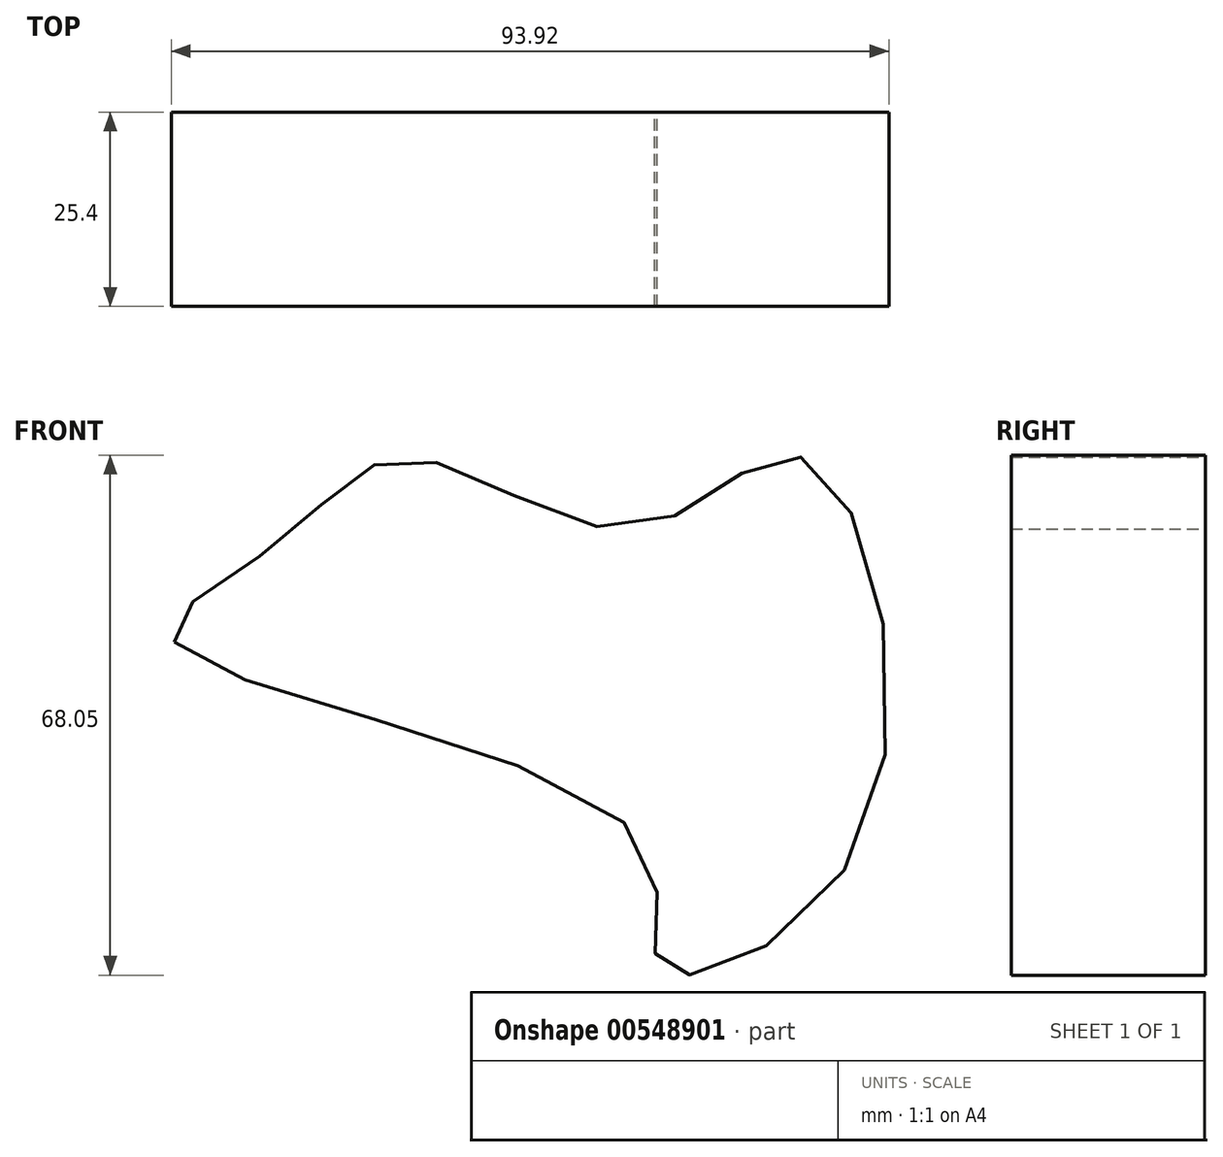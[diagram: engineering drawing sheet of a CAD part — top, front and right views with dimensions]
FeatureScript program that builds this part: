
annotation { "Feature Type Name" : "Feature", "Feature Type Description" : "" }
export const myFeature = defineFeature(function(context is Context, id is Id, definition is map)
    precondition{}
    {
        {
            var Q0;
            Q0=qCreatedBy(makeId("Front.planeOp"),FACE);
            var sketch = newSketch(context, id + "F0", { "sketchPlane" : qUnion([Q0])});
            skPoint(sketch, "E0", {"position": v(-36.04, 5.71) * mm});
            skPoint(sketch, "E1", {"position": v(-22.85, 18.46) * mm});
            skPoint(sketch, "E2", {"position": v(-5.27, 29.89) * mm});
            skPoint(sketch, "E3", {"position": v(24.61, 20.66) * mm});
            skPoint(sketch, "E4", {"position": v(24.61, -19.78) * mm});
            skFitSpline(sketch, "E5", {"points": [v(-36.04, 5.71) * mm, v(-22.85, 18.46) * mm, v(-5.27, 29.89) * mm, v(24.61, 20.66) * mm, v(46.15, 29.89) * mm, v(53.62, -20.66) * mm, v(27.69, -36.92) * mm, v(24.61, -19.78) * mm, v(-36.04, 5.71) * mm]});
            skSolve(sketch);
        }
        {
            var Q0;
            Q0 = qSketchRegion(id + "F0", true);
            extrude(context, id + "F1", {"entities" : qUnion([Q0]), "depth" : 25.4 * mm, "offsetDistance" : 25.4 * mm});
        }
    });
